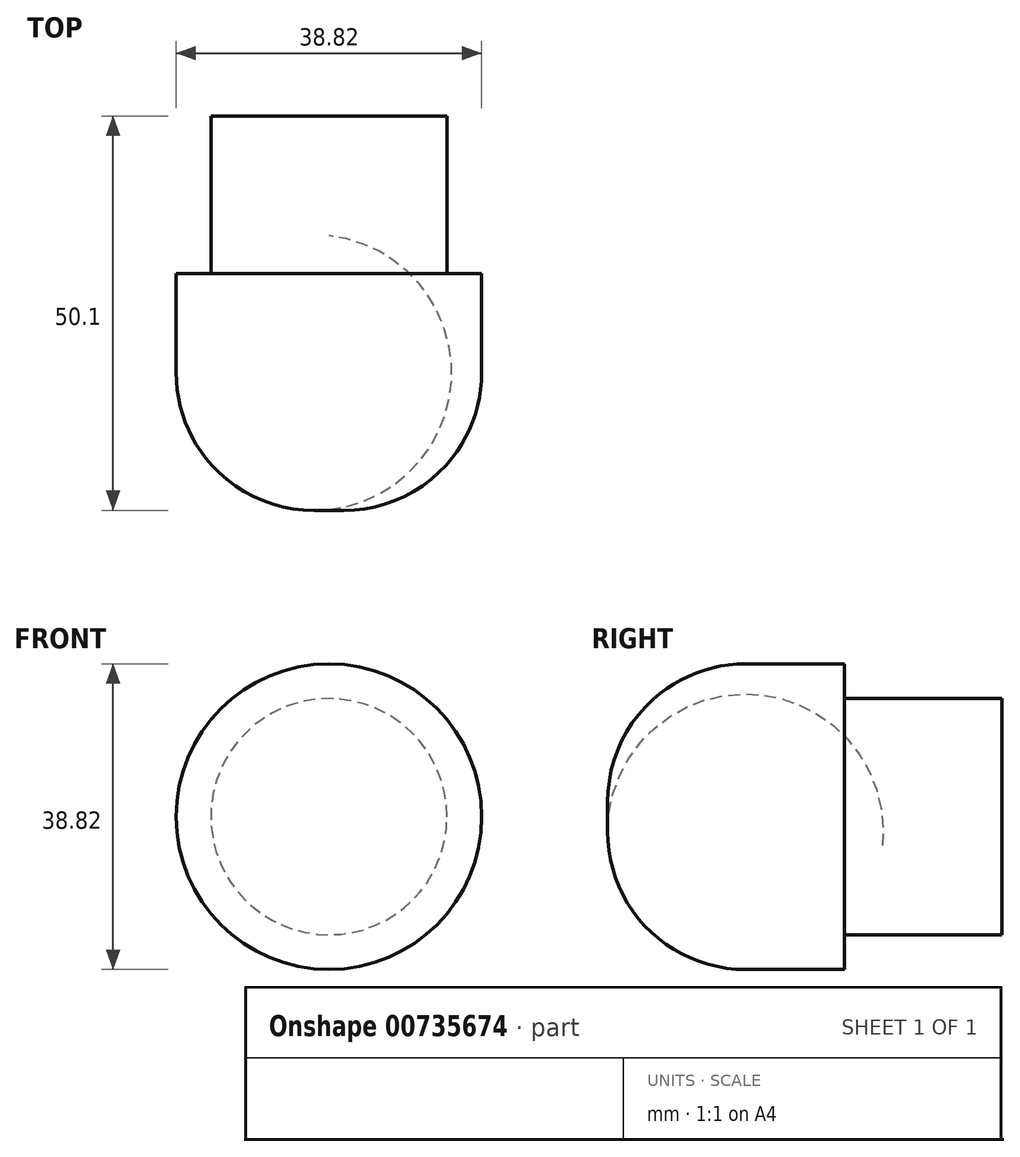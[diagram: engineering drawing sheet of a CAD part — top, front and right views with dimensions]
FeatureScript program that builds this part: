
annotation { "Feature Type Name" : "Feature", "Feature Type Description" : "" }
export const myFeature = defineFeature(function(context is Context, id is Id, definition is map)
    precondition{}
    {
        {
            var Q0;
            Q0=qCreatedBy(makeId("Top.planeOp"),FACE);
            var sketch = newSketch(context, id + "F0", { "sketchPlane" : qUnion([Q0])});
            skLineSegment(sketch, "E0", {"start": v(0, 0) * mm, "end": v(0, 50) * mm});
            skLineSegment(sketch, "E1", {"start": v(0, 50) * mm, "end": v(15, 50) * mm});
            skLineSegment(sketch, "E2", {"start": v(15, 50) * mm, "end": v(15, 30) * mm});
            skLineSegment(sketch, "E3", {"start": v(15, 30) * mm, "end": v(19.4, 30) * mm});
            skLineSegment(sketch, "E4", {"start": v(19.4, 30) * mm, "end": v(19.4, 17.4) * mm});
            skArc(sketch, "E5", {"start": v(19.4, 17.4) * mm, "mid": v(13.59, 4.36) * mm, "end": v(0, 0) * mm});
            skSolve(sketch);
        }
        {
            var Q0;
            Q0 = qSketchRegion(id + "F0", true);
            var Q1;
            Q1=sQuery(id+"F0.wireOp",EDGE,"E0");
            revolve(context, id + "F1", {"surfaceOperationType" : NewSurfaceOperationType.NEW, "entities" : qUnion([Q0]), "axis" : qUnion([Q1]), "revolveType" : RevolveType.FULL});
        }
    });
